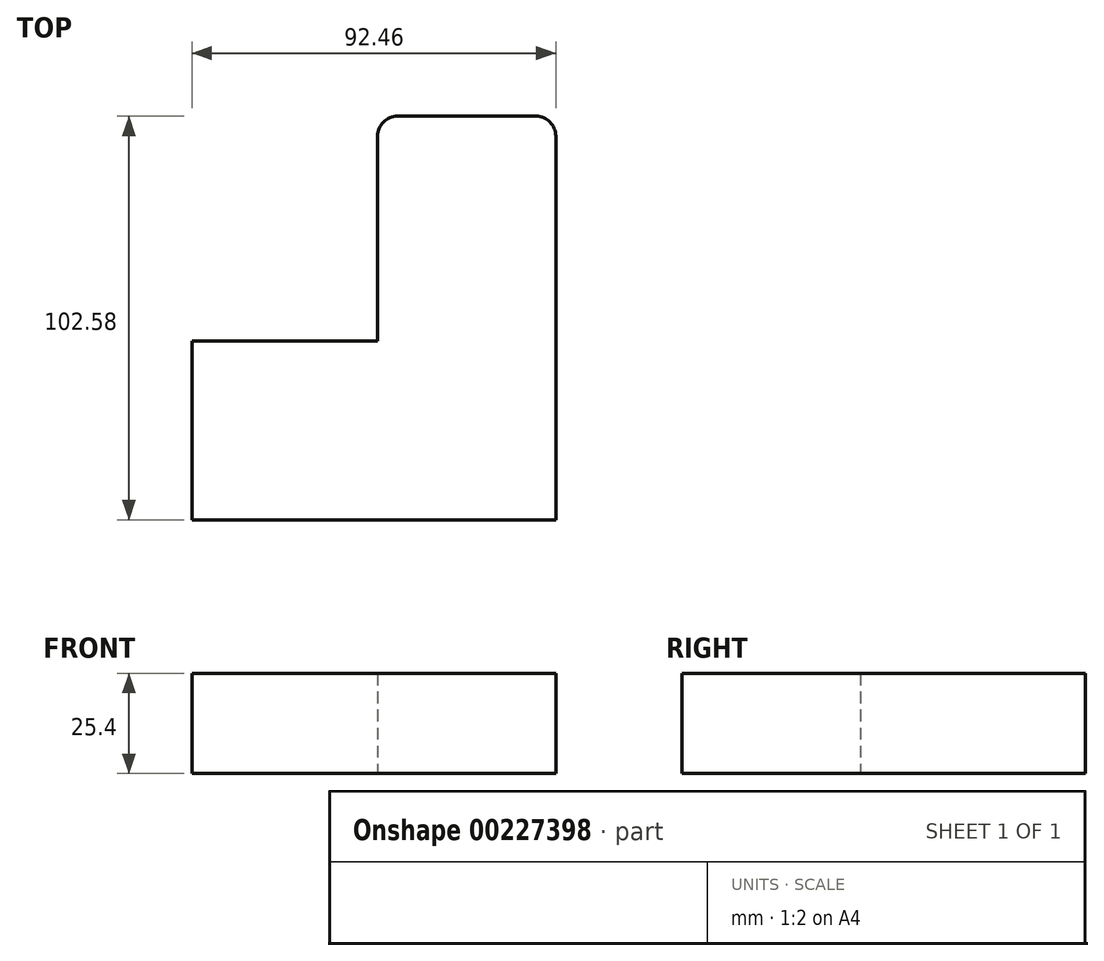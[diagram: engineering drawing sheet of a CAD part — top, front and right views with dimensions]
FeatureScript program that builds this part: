
annotation { "Feature Type Name" : "Feature", "Feature Type Description" : "" }
export const myFeature = defineFeature(function(context is Context, id is Id, definition is map)
    precondition{}
    {
        {
            var Q0;
            Q0=qCreatedBy(makeId("Top.planeOp"),FACE);
            var sketch = newSketch(context, id + "F0", { "sketchPlane" : qUnion([Q0])});
            skLineSegment(sketch, "E0", {"start": v(0, 0) * mm, "end": v(0, 57.17) * mm});
            skLineSegment(sketch, "E1", {"start": v(0, 57.17) * mm, "end": v(45.27, 57.17) * mm});
            skLineSegment(sketch, "E2", {"start": v(45.27, 57.17) * mm, "end": v(45.27, -45.4) * mm});
            skLineSegment(sketch, "E3", {"start": v(45.27, -45.4) * mm, "end": v(-47.19, -45.4) * mm});
            skLineSegment(sketch, "E4", {"start": v(-47.19, -45.4) * mm, "end": v(-47.19, 0) * mm});
            skLineSegment(sketch, "E5", {"start": v(-47.19, 0) * mm, "end": v(0, 0) * mm});
            skSolve(sketch);
        }
        {
            var Q0;
            Q0 = qSketchRegion(id + "F0", true);
            extrude(context, id + "F1", {"entities" : qUnion([Q0]), "endBound" : BoundingType.SYMMETRIC, "depth" : 25.4 * mm});
        }
        {
            var Q0;
            Q0=makeQuery(id+"F1.opExtrude","SWEPT_EDGE",EDGE,{"disambiguationData":[OSD([sQuery(id+"F0.wireOp",EDGE,"E0"),sQuery(id+"F0.wireOp",EDGE,"E1")])]});
            var Q1;
            Q1=makeQuery(id+"F1.opExtrude","SWEPT_EDGE",EDGE,{"disambiguationData":[OSD([sQuery(id+"F0.wireOp",EDGE,"E1"),sQuery(id+"F0.wireOp",EDGE,"E2")])]});
            fillet(context, id + "F2", {"entities" : qUnion([Q0, Q1]), "radius" : 5.08 * mm, "tangentPropagation" : true, "allowEdgeOverflow" : false});
        }
    });
